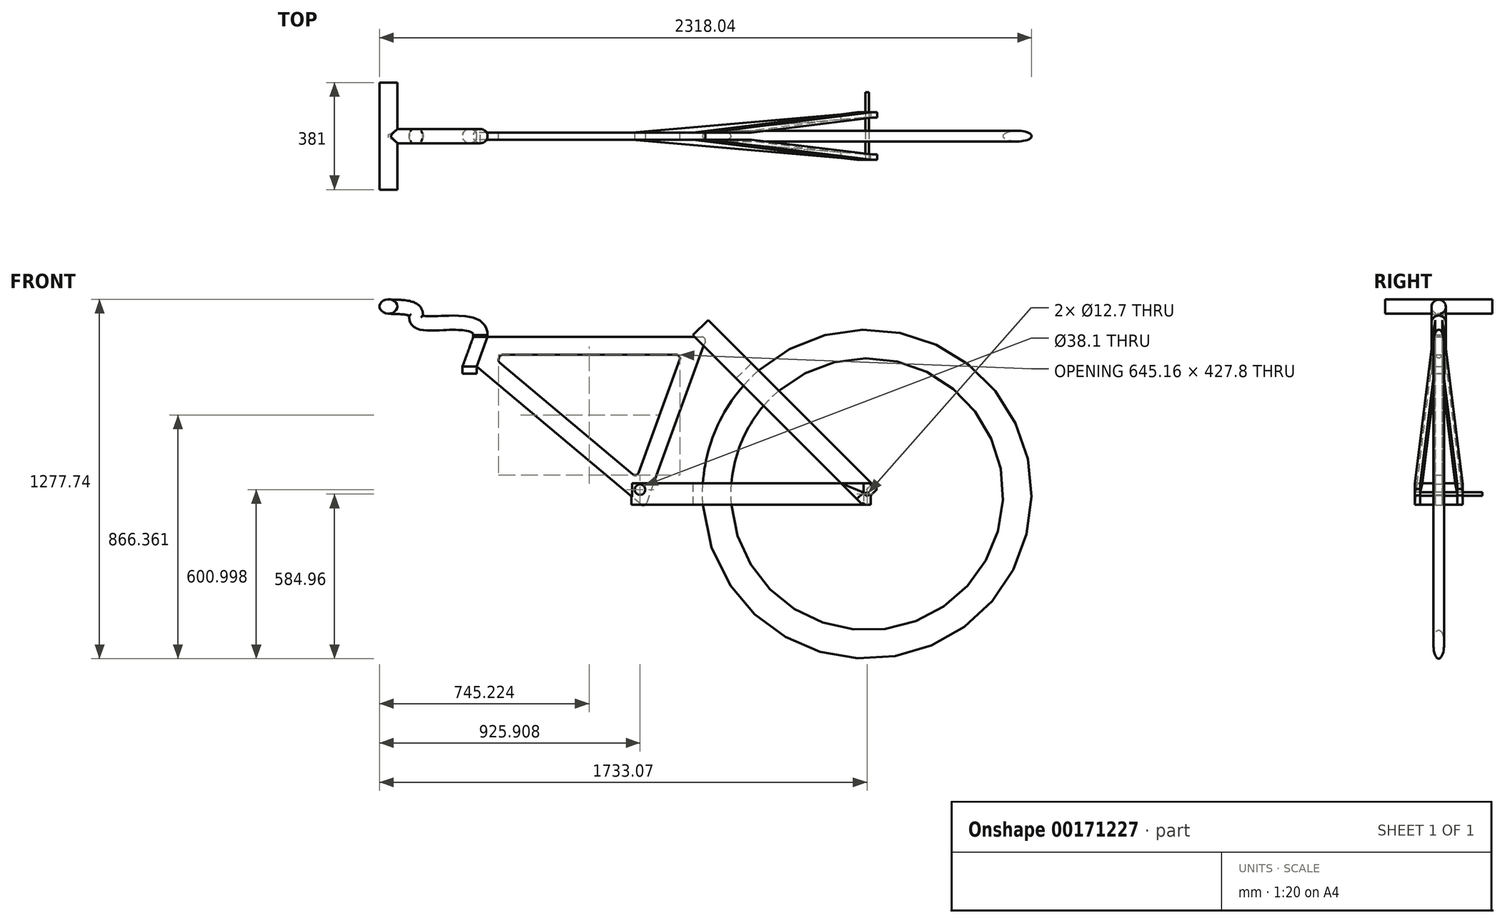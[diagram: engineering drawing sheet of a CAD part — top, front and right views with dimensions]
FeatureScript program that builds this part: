
annotation { "Feature Type Name" : "Feature", "Feature Type Description" : "" }
export const myFeature = defineFeature(function(context is Context, id is Id, definition is map)
    precondition{}
    {
        {
            var Q0;
            Q0=qCreatedBy(makeId("Front.planeOp"),FACE);
            var sketch = newSketch(context, id + "F0", { "sketchPlane" : qUnion([Q0])});
            skLineSegment(sketch, "E0", {"start": v(491.06, -430.17) * mm, "end": v(-92.67, 59.64) * mm});
            skLineSegment(sketch, "E1", {"start": v(-54.29, 165.1) * mm, "end": v(707.71, 165.1) * mm});
            skLineSegment(sketch, "E2", {"start": v(719.65, 148.06) * mm, "end": v(511.15, -424.78) * mm});
            skLineSegment(sketch, "E3", {"start": v(-54.29, 165.1) * mm, "end": v(-92.67, 59.64) * mm});
            skLineSegment(sketch, "E4.0", {"start": v(-0.93, 101.6) * mm, "end": v(617.03, 101.6) * mm});
            skLineSegment(sketch, "E4.1", {"start": v(-12.86, 93.24) * mm, "end": v(-14.75, 88.06) * mm});
            skLineSegment(sketch, "E4.2", {"start": v(462.4, -323.23) * mm, "end": v(-10.98, 73.99) * mm});
            skLineSegment(sketch, "E4.3", {"start": v(628.96, 84.56) * mm, "end": v(482.5, -317.84) * mm});
            skPoint(sketch, "E5.visualSharp", {"position": v(-17.8, 79.7) * mm});
            skArc(sketch, "E5.filletArc", {"start": v(-14.75, 88.06) * mm, "mid": v(-15.08, 80.43) * mm, "end": v(-10.98, 73.99) * mm});
            skPoint(sketch, "E6.visualSharp", {"position": v(-9.82, 101.6) * mm});
            skArc(sketch, "E6.filletArc", {"start": v(-0.93, 101.6) * mm, "mid": v(-8.21, 99.3) * mm, "end": v(-12.86, 93.24) * mm});
            skPoint(sketch, "E7.visualSharp", {"position": v(635.16, 101.6) * mm});
            skArc(sketch, "E7.filletArc", {"start": v(628.96, 84.56) * mm, "mid": v(627.43, 96.18) * mm, "end": v(617.03, 101.6) * mm});
            skPoint(sketch, "E8.visualSharp", {"position": v(476.3, -334.89) * mm});
            skArc(sketch, "E8.filletArc", {"start": v(462.4, -323.23) * mm, "mid": v(473.85, -325.77) * mm, "end": v(482.5, -317.84) * mm});
            skPoint(sketch, "E9.visualSharp", {"position": v(504.95, -441.82) * mm});
            skArc(sketch, "E9.filletArc", {"start": v(491.06, -430.17) * mm, "mid": v(502.5, -432.7) * mm, "end": v(511.15, -424.78) * mm});
            skPoint(sketch, "E10.visualSharp", {"position": v(725.85, 165.1) * mm});
            skArc(sketch, "E10.filletArc", {"start": v(719.65, 148.06) * mm, "mid": v(718.12, 159.68) * mm, "end": v(707.71, 165.1) * mm});
            skSolve(sketch);
        }
        {
            var Q0;
            Q0=makeQuery(id+"F0.imprint","IMPRINT",FACE,{"disambiguationData":[TD([[makeQuery(id+"F0.imprint","IMPRINT",EDGE,{"derivedFrom":sQuery(id+"F0.wireOp",EDGE,"E0")}),-1.0]])]});
            extrude(context, id + "F1", {"entities" : qUnion([Q0]), "endBound" : BoundingType.SYMMETRIC, "depth" : 25.4 * mm});
        }
        {
            var Q0;
            Q0=makeQuery(id+"F1.opExtrude","SWEPT_FACE",FACE,{"disambiguationData":[OSD([sQuery(id+"F0.wireOp",EDGE,"E1")])]});
            var sketch = newSketch(context, id + "F2", { "sketchPlane" : qUnion([Q0])});
            skArc(sketch, "E11", {"start": v(-64.45, 20.32) * mm, "mid": v(-105.09, 0) * mm, "end": v(-64.45, -20.32) * mm});
            skCircle(sketch, "E12", {"center": v(-79.69, 0) * mm, "radius": 19.05 * mm});
            skLineSegment(sketch, "E13", {"start": v(-54.29, -12.7) * mm, "end": v(-64.45, -20.32) * mm});
            skLineSegment(sketch, "E14", {"start": v(-54.29, 12.7) * mm, "end": v(-64.45, 20.32) * mm});
            skSolve(sketch);
        }
        {
            var Q0;
            Q0=makeQuery(id+"F2.imprint","IMPRINT",FACE,{"disambiguationData":[TD([[makeQuery(id+"F2.imprint","IMPRINT",EDGE,{"derivedFrom":sQuery(id+"F2.wireOp",EDGE,"E11")}),1.0]])]});
            var Q1;
            Q1=makeQuery(id+"F1.opExtrude","CAP_EDGE",EDGE,{"disambiguationData":[OSD([sQuery(id+"F0.wireOp",EDGE,"E3")])],"isStart":false});
            sweep(context, id + "F3", {"operationType" : NewBodyOperationType.ADD, "profiles" : qUnion([Q0]), "path" : qUnion([Q1])});
        }
        {
            var Q0;
            {var subQ0=sQuery(id+"F0.wireOp",EDGE,"E1");Q0=makeQuery(id+"F3.boolean.opBoolean","MERGE",FACE,{"derivedFrom":[makeQuery(id+"F1.opExtrude","SWEPT_FACE",FACE,{"disambiguationData":[OSD([subQ0])]}),makeQuery(id+"F3.opSweep","CAP_FACE",FACE,{"disambiguationData":[OSD([subQ0,sQuery(id+"F0.wireOp",EDGE,"E3"),sQuery(id+"F2.wireOp",EDGE,"E11"),sQuery(id+"F2.wireOp",EDGE,"E12"),sQuery(id+"F2.wireOp",EDGE,"E13"),sQuery(id+"F2.wireOp",EDGE,"E14")])],"isStart":true})]});}
            var sketch = newSketch(context, id + "F4", { "sketchPlane" : qUnion([Q0])});
            skCircle(sketch, "E15", {"center": v(-79.69, 0) * mm, "radius": 19.05 * mm});
            skSolve(sketch);
        }
        {
            var Q0;
            Q0 = qSketchRegion(id + "F4", true);
            var Q1;
            Q1=makeQuery(id+"F3.opSweep","SWEPT_EDGE",EDGE,{"disambiguationData":[OSD([sQuery(id+"F0.wireOp",EDGE,"E3"),sQuery(id+"F2.wireOp",EDGE,"E11"),sQuery(id+"F2.wireOp",EDGE,"E13")])]});
            sweep(context, id + "F5", {"profiles" : qUnion([Q0]), "path" : qUnion([Q1])});
        }
        {
            var Q0;
            Q0=makeQuery(id+"F5.opSweep","CAP_FACE",FACE,{"disambiguationData":[OSD([sQuery(id+"F0.wireOp",EDGE,"E3"),sQuery(id+"F2.wireOp",EDGE,"E11"),sQuery(id+"F2.wireOp",EDGE,"E13"),sQuery(id+"F4.wireOp",EDGE,"E15")])],"isStart":true});
            var sketch = newSketch(context, id + "F6", { "sketchPlane" : qUnion([Q0])});
            skCircle(sketch, "E16", {"center": v(-79.69, 0) * mm, "radius": 25.4 * mm});
            skSolve(sketch);
        }
        {
            var Q0;
            Q0 = qSketchRegion(id + "F6", true);
            extrude(context, id + "F7", {"entities" : qUnion([Q0]), "operationType" : NewBodyOperationType.ADD, "depth" : 6.35 * mm});
        }
        {
            var Q0;
            Q0=qCreatedBy(makeId("Right.planeOp"),FACE);
            cPlane(context, id + "F8", {"entities" : qUnion([Q0]), "cplaneType" : CPlaneType.OFFSET, "offset" : 406.4 * mm, "oppositeDirection" : true, "width" : 152.4 * mm, "height" : 152.4 * mm});
        }
        {
            var Q0;
            Q0=qCreatedBy(id+"F8.planeOp",FACE);
            var sketch = newSketch(context, id + "F9", { "sketchPlane" : qUnion([Q0])});
            skCircle(sketch, "E17", {"center": v(0, 273.05) * mm, "radius": 25.4 * mm});
            skSolve(sketch);
        }
        {
            var Q0;
            Q0=qCreatedBy(makeId("Front.planeOp"),FACE);
            var sketch = newSketch(context, id + "F10", { "sketchPlane" : qUnion([Q0])});
            skFitSpline(sketch, "E18", {"points": [v(-79.69, 171.45) * mm, v(-295.21, 218.05) * mm, v(-313.96, 257.15) * mm, v(-406.4, 273.05) * mm], "startDerivative": vector(16.07, 463.7) * mm, "endDerivative": vector(-252.17, 9.4) * mm});
            skSolve(sketch);
        }
        {
            var Q0;
            Q0=makeQuery(id+"F9.imprint","IMPRINT",FACE,{"disambiguationData":[TD([[makeQuery(id+"F9.imprint","IMPRINT",EDGE,{"derivedFrom":sQuery(id+"F9.wireOp",EDGE,"E17")}),1.0]])]});
            var Q1;
            Q1=sQuery(id+"F10.wireOp",EDGE,"E18");
            sweep(context, id + "F11", {"operationType" : NewBodyOperationType.ADD, "profiles" : qUnion([Q0]), "path" : qUnion([Q1])});
        }
        {
            var Q0;
            Q0=qCreatedBy(makeId("Top.planeOp"),FACE);
            cPlane(context, id + "F12", {"entities" : qUnion([Q0]), "cplaneType" : CPlaneType.OFFSET, "offset" : 254 * mm, "width" : 152.4 * mm, "height" : 152.4 * mm});
        }
        {
            var Q0;
            Q0=qCreatedBy(makeId("Front.planeOp"),FACE);
            var sketch = newSketch(context, id + "F13", { "sketchPlane" : qUnion([Q0])});
            skEllipse(sketch, "E19", {"center": v(-406.4, 273.68) * mm, "majorRadius": 31.75 * mm, "minorRadius": 25.4 * mm, "majorAxis": v(1, 0)});
            skSolve(sketch);
        }
        {
            var Q0;
            Q0 = qSketchRegion(id + "F13", true);
            extrude(context, id + "F14", {"entities" : qUnion([Q0]), "operationType" : NewBodyOperationType.ADD, "endBound" : BoundingType.SYMMETRIC, "depth" : 381 * mm});
        }
        {
            var Q0;
            Q0=makeQuery(id+"F1.opExtrude","CAP_FACE",FACE,{"disambiguationData":[OSD([sQuery(id+"F0.wireOp",EDGE,"E0"),sQuery(id+"F0.wireOp",EDGE,"E1"),sQuery(id+"F0.wireOp",EDGE,"E2"),sQuery(id+"F0.wireOp",EDGE,"E3"),sQuery(id+"F0.wireOp",EDGE,"E4.0"),sQuery(id+"F0.wireOp",EDGE,"E4.1"),sQuery(id+"F0.wireOp",EDGE,"E4.2"),sQuery(id+"F0.wireOp",EDGE,"E4.3"),sQuery(id+"F0.wireOp",EDGE,"E5.filletArc"),sQuery(id+"F0.wireOp",EDGE,"E6.filletArc"),sQuery(id+"F0.wireOp",EDGE,"E7.filletArc"),sQuery(id+"F0.wireOp",EDGE,"E8.filletArc"),sQuery(id+"F0.wireOp",EDGE,"E9.filletArc"),sQuery(id+"F0.wireOp",EDGE,"E10.filletArc")])],"isStart":false});
            var sketch = newSketch(context, id + "F15", { "sketchPlane" : qUnion([Q0])});
            skCircle(sketch, "E20", {"center": v(487.76, -377.66) * mm, "radius": 19.05 * mm});
            skSolve(sketch);
        }
        {
            var Q0;
            Q0=qCreatedBy(makeId("Top.planeOp"),FACE);
            cPlane(context, id + "F16", {"entities" : qUnion([Q0]), "cplaneType" : CPlaneType.OFFSET, "offset" : 431.8 * mm, "oppositeDirection" : true, "width" : 152.4 * mm, "height" : 152.4 * mm});
        }
        {
            var Q0;
            Q0=qCreatedBy(id+"F16.planeOp",FACE);
            var sketch = newSketch(context, id + "F17", { "sketchPlane" : qUnion([Q0])});
            skLineSegment(sketch, "E21", {"start": v(457.2, -12.51) * mm, "end": v(1282.22, -84.7) * mm});
            skLineSegment(sketch, "E22", {"start": v(1282.22, -65.64) * mm, "end": v(674.94, -12.51) * mm});
            skLineSegment(sketch, "E23", {"start": v(674.94, -12.51) * mm, "end": v(457.2, -12.51) * mm});
            skLineSegment(sketch, "E24.MirrorCS", {"start": v(1282.22, 65.64) * mm, "end": v(674.94, 12.51) * mm});
            skLineSegment(sketch, "E25.MirrorCS", {"start": v(457.2, 12.51) * mm, "end": v(1282.22, 84.7) * mm});
            skLineSegment(sketch, "E26.MirrorCS", {"start": v(674.94, 12.51) * mm, "end": v(457.2, 12.51) * mm});
            skLineSegment(sketch, "E27.bottom", {"start": v(1282.22, -84.7) * mm, "end": v(1307.62, -84.7) * mm});
            skLineSegment(sketch, "E27.top", {"start": v(1282.22, -65.64) * mm, "end": v(1307.62, -65.64) * mm});
            skLineSegment(sketch, "E27.right", {"start": v(1307.62, -84.7) * mm, "end": v(1307.62, -65.64) * mm});
            skLineSegment(sketch, "E28.MirrorCS", {"start": v(1282.22, 84.7) * mm, "end": v(1307.62, 84.7) * mm});
            skLineSegment(sketch, "E29.MirrorCS", {"start": v(1282.22, 65.64) * mm, "end": v(1307.62, 65.64) * mm});
            skLineSegment(sketch, "E30.MirrorCS", {"start": v(1307.62, 84.7) * mm, "end": v(1307.62, 65.64) * mm});
            skPoint(sketch, "E31.MirrorCS.end.orphan", {"position": v(1282.22, 65.64) * mm});
            skPoint(sketch, "E31.MirrorCS.start.orphan", {"position": v(1282.22, 84.7) * mm});
            skSolve(sketch);
        }
        {
            var Q0;
            Q0 = qSketchRegion(id + "F17", true);
            extrude(context, id + "F18", {"entities" : qUnion([Q0]), "depth" : 76.2 * mm});
        }
        {
            var Q0;
            Q0=makeQuery(id+"F18.opExtrude","SWEPT_FACE",FACE,{"disambiguationData":[OSD([sQuery(id+"F17.wireOp",EDGE,"E27.bottom")])]});
            var sketch = newSketch(context, id + "F19", { "sketchPlane" : qUnion([Q0])});
            skCircle(sketch, "E32", {"center": v(1294.92, -393.7) * mm, "radius": 6.35 * mm});
            skPoint(sketch, "E32.centerSnap0", {"position": v(1282.22, -393.7) * mm});
            skPoint(sketch, "E32.centerSnap1", {"position": v(1294.92, -431.8) * mm});
            skSolve(sketch);
        }
        {
            var Q0;
            Q0 = qSketchRegion(id + "F19", true);
            extrude(context, id + "F20", {"entities" : qUnion([Q0]), "operationType" : NewBodyOperationType.REMOVE, "endBound" : BoundingType.THROUGH_ALL, "oppositeDirection" : true, "depth" : 25.4 * mm});
        }
        {
            var Q0;
            Q0=makeQuery(id+"F18.opExtrude","SWEPT_BODY",BODY,{"disambiguationData":[OSD([sQuery(id+"F17.wireOp",EDGE,"E21"),sQuery(id+"F17.wireOp",EDGE,"E22"),sQuery(id+"F17.wireOp",EDGE,"E23"),sQuery(id+"F17.wireOp",EDGE,"E27.bottom"),sQuery(id+"F17.wireOp",EDGE,"E27.top"),sQuery(id+"F17.wireOp",EDGE,"E27.right")])]});
            var Q1;
            Q1=makeQuery(id+"F18.opExtrude","SWEPT_BODY",BODY,{"disambiguationData":[OSD([sQuery(id+"F17.wireOp",EDGE,"E24.MirrorCS"),sQuery(id+"F17.wireOp",EDGE,"E25.MirrorCS"),sQuery(id+"F17.wireOp",EDGE,"E26.MirrorCS"),sQuery(id+"F17.wireOp",EDGE,"E28.MirrorCS"),sQuery(id+"F17.wireOp",EDGE,"E29.MirrorCS"),sQuery(id+"F17.wireOp",EDGE,"E30.MirrorCS")])]});
            var Q2;
            Q2=makeQuery(id+"F20.boolean.opBoolean","INTERSECT",EDGE,{"derivedFrom":[makeQuery(id+"F18.opExtrude","SWEPT_FACE",FACE,{"disambiguationData":[OSD([sQuery(id+"F17.wireOp",EDGE,"E27.top")])]}),makeQuery(id+"F20.opExtrude","SWEPT_FACE",FACE,{"disambiguationData":[OSD([sQuery(id+"F19.wireOp",EDGE,"E32")])]})]});
            circularPattern(context, id + "F21", {"operationType" : NewBodyOperationType.ADD, "entities" : qUnion([Q0, Q1]), "axis" : qUnion([Q2]), "angle" : 45 * degree, "instanceCount" : 2});
        }
        {
            var Q0;
            Q0 = qSketchRegion(id + "F15", true);
            extrude(context, id + "F22", {"entities" : qUnion([Q0]), "operationType" : NewBodyOperationType.REMOVE, "endBound" : BoundingType.SYMMETRIC, "oppositeDirection" : true, "depth" : 76.2 * mm});
        }
        {
            var Q0;
            {var subQ0=makeQuery(id+"F18.opExtrude","SWEPT_FACE",FACE,{"disambiguationData":[OSD([sQuery(id+"F17.wireOp",EDGE,"E27.bottom")])]});Q0=makeQuery(id+"F21.boolean.opBoolean","MERGE",FACE,{"derivedFrom":[subQ0,makeQuery(id+"F21.opPattern","COPY",FACE,{"derivedFrom":subQ0,"instanceName":"1"})]});}
            var sketch = newSketch(context, id + "F23", { "sketchPlane" : qUnion([Q0])});
            skCircle(sketch, "E33", {"center": v(1294.92, -393.7) * mm, "radius": 6.35 * mm});
            skSolve(sketch);
        }
        {
            var Q0;
            Q0 = qSketchRegion(id + "F23", true);
            extrude(context, id + "F24", {"entities" : qUnion([Q0]), "oppositeDirection" : true, "depth" : 240.03 * mm});
        }
        {
            var Q0;
            Q0=makeQuery(id+"F5.opSweep","CAP_FACE",FACE,{"disambiguationData":[OSD([sQuery(id+"F0.wireOp",EDGE,"E3"),sQuery(id+"F2.wireOp",EDGE,"E11"),sQuery(id+"F2.wireOp",EDGE,"E13"),sQuery(id+"F4.wireOp",EDGE,"E15")])],"isStart":false});
            var sketch = newSketch(context, id + "F25", { "sketchPlane" : qUnion([Q0])});
            skCircle(sketch, "E34", {"center": v(-118.07, 0) * mm, "radius": 25.4 * mm});
            skSolve(sketch);
        }
        {
            var Q0;
            Q0 = qSketchRegion(id + "F25", true);
            extrude(context, id + "F26", {"entities" : qUnion([Q0]), "operationType" : NewBodyOperationType.ADD, "depth" : 25.4 * mm});
        }
        {
            var Q0;
            Q0=qCreatedBy(id+"F16.planeOp",FACE);
            var sketch = newSketch(context, id + "F27", { "sketchPlane" : qUnion([Q0])});
            skEllipse(sketch, "E35", {"center": v(762, 0) * mm, "majorRadius": 50.8 * mm, "minorRadius": 19.05 * mm, "majorAxis": v(1, 0)});
            skSolve(sketch);
        }
        {
            var Q0;
            Q0 = qSketchRegion(id + "F27", true);
            var Q1;
            Q1=makeQuery(id+"F24.opExtrude","SWEPT_FACE",FACE,{"disambiguationData":[OSD([sQuery(id+"F23.wireOp",EDGE,"E33")])]});
            revolve(context, id + "F28", {"entities" : qUnion([Q0]), "axis" : qUnion([Q1]), "revolveType" : RevolveType.FULL});
        }
    });
